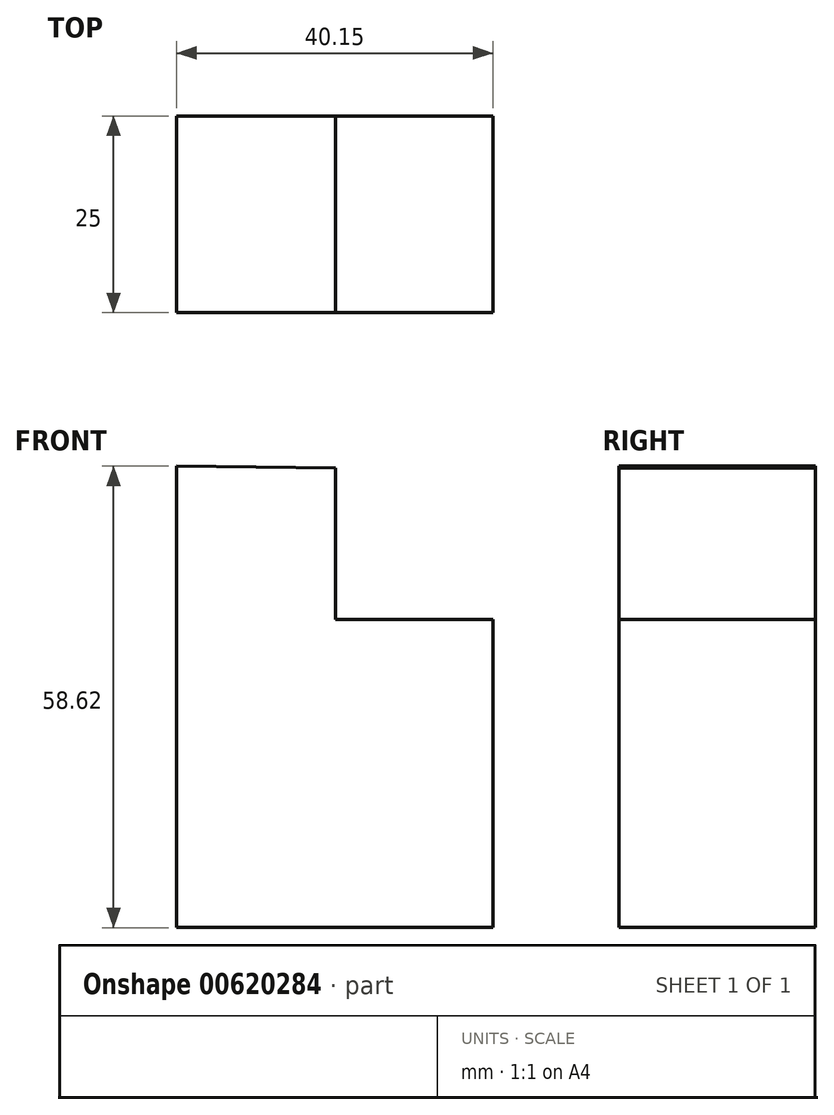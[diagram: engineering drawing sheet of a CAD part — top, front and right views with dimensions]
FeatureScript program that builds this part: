
annotation { "Feature Type Name" : "Feature", "Feature Type Description" : "" }
export const myFeature = defineFeature(function(context is Context, id is Id, definition is map)
    precondition{}
    {
        {
            var Q0;
            Q0=qCreatedBy(makeId("Front.planeOp"),FACE);
            var sketch = newSketch(context, id + "F0", { "sketchPlane" : qUnion([Q0])});
            skLineSegment(sketch, "E0", {"start": v(-49.09, 51.65) * mm, "end": v(-49.09, -6.97) * mm});
            skLineSegment(sketch, "E1", {"start": v(-49.09, -6.97) * mm, "end": v(-8.94, -6.97) * mm});
            skLineSegment(sketch, "E2", {"start": v(-8.94, -6.97) * mm, "end": v(-8.94, 32.17) * mm});
            skLineSegment(sketch, "E3", {"start": v(-8.94, 32.17) * mm, "end": v(-28.94, 32.17) * mm});
            skLineSegment(sketch, "E4", {"start": v(-28.94, 32.17) * mm, "end": v(-28.94, 51.4) * mm});
            skLineSegment(sketch, "E5", {"start": v(-28.94, 51.4) * mm, "end": v(-49.09, 51.65) * mm});
            skSolve(sketch);
        }
        {
            var Q0;
            Q0 = qSketchRegion(id + "F0", true);
            extrude(context, id + "F1", {"entities" : qUnion([Q0]), "depth" : 25 * mm, "offsetDistance" : 25 * mm});
        }
    });
